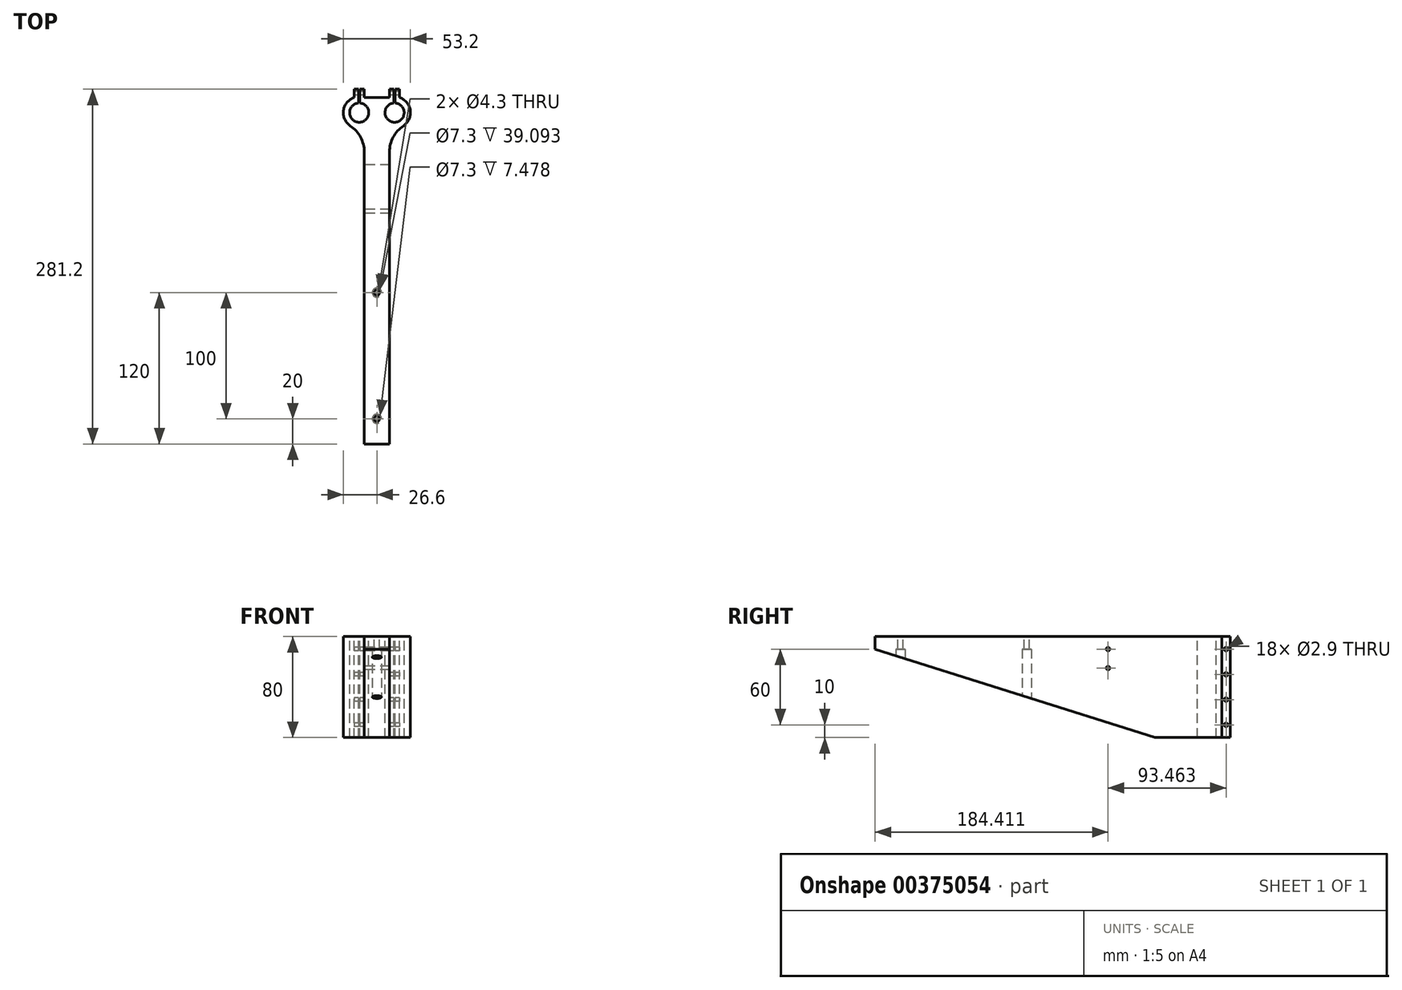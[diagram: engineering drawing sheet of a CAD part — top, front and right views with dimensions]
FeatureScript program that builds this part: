
annotation { "Feature Type Name" : "Feature", "Feature Type Description" : "" }
export const myFeature = defineFeature(function(context is Context, id is Id, definition is map)
    precondition{}
    {
        {
            var Q0;
            Q0=qCreatedBy(makeId("Top.planeOp"),FACE);
            var sketch = newSketch(context, id + "F0", { "sketchPlane" : qUnion([Q0])});
            skCircle(sketch, "E0", {"center": v(0, 0) * mm, "radius": 7.6 * mm});
            skArc(sketch, "E1.0", {"start": v(-4, 11.95) * mm, "mid": v(-12.49, 1.7) * mm, "end": v(-7.04, -10.45) * mm});
            skLineSegment(sketch, "E2.top", {"start": v(4, 18.6) * mm, "end": v(-4, 18.6) * mm});
            skLineSegment(sketch, "E2.left", {"start": v(4, 11.95) * mm, "end": v(4, 18.6) * mm});
            skLineSegment(sketch, "E2.right", {"start": v(-4, 11.95) * mm, "end": v(-4, 18.6) * mm});
            skPoint(sketch, "E2.middle", {"position": v(0, 12.6) * mm});
            skLineSegment(sketch, "E3.top", {"start": v(4, -262.6) * mm, "end": v(24, -262.6) * mm});
            skCircle(sketch, "E4", {"center": v(28, 0) * mm, "radius": 7.6 * mm});
            skArc(sketch, "E5.0", {"start": v(35.04, -10.45) * mm, "mid": v(40.49, 1.7) * mm, "end": v(32, 11.95) * mm});
            skLineSegment(sketch, "E6.bottom", {"start": v(24, 18.6) * mm, "end": v(32, 18.6) * mm});
            skLineSegment(sketch, "E6.left", {"start": v(24, 18.6) * mm, "end": v(24, 11.95) * mm});
            skLineSegment(sketch, "E6.right", {"start": v(32, 18.6) * mm, "end": v(32, 11.95) * mm});
            skLineSegment(sketch, "E7", {"start": v(4, 11.95) * mm, "end": v(24, 11.95) * mm});
            skLineSegment(sketch, "E8", {"start": v(4, -31.19) * mm, "end": v(4, -262.6) * mm});
            skLineSegment(sketch, "E9", {"start": v(24, -262.6) * mm, "end": v(24, -31.19) * mm});
            skPoint(sketch, "E10.visualSharp", {"position": v(4, -11.95) * mm});
            skArc(sketch, "E10.filletArc", {"start": v(4, -31.19) * mm, "mid": v(1.07, -19.44) * mm, "end": v(-7.04, -10.45) * mm});
            skPoint(sketch, "E11.visualSharp", {"position": v(24, -11.95) * mm});
            skArc(sketch, "E11.filletArc", {"start": v(35.04, -10.45) * mm, "mid": v(26.93, -19.44) * mm, "end": v(24, -31.19) * mm});
            skSolve(sketch);
        }
        {
            var Q0;
            Q0=makeQuery(id+"F0.imprint","IMPRINT",FACE,{"disambiguationData":[TD([[makeQuery(id+"F0.imprint","IMPRINT",EDGE,{"derivedFrom":sQuery(id+"F0.wireOp",EDGE,"E3.top")}),1.0]])]});
            extrude(context, id + "F1", {"entities" : qUnion([Q0]), "oppositeDirection" : true, "depth" : 80 * mm});
        }
        {
            var Q0;
            Q0=makeQuery(id+"F0.imprint","IMPRINT",FACE,{"disambiguationData":[TD([[makeQuery(id+"F0.imprint","IMPRINT",EDGE,{"derivedFrom":sQuery(id+"F0.wireOp",EDGE,"E0")}),-1.0]])]});
            extrude(context, id + "F2", {"entities" : qUnion([Q0]), "operationType" : NewBodyOperationType.ADD, "oppositeDirection" : true, "depth" : 80 * mm});
        }
        {
            var Q0;
            {var subQ0=sQuery(id+"F0.wireOp",EDGE,"E1.0");Q0=makeQuery(id+"F2.boolean.opBoolean","MERGE",FACE,{"derivedFrom":[makeQuery(id+"F1.opExtrude","CAP_FACE",FACE,{"disambiguationData":[OSD([subQ0,sQuery(id+"F0.wireOp",EDGE,"E3.top"),sQuery(id+"F0.wireOp",EDGE,"E3.left"),sQuery(id+"F0.wireOp",EDGE,"E3.right")])],"isStart":true}),makeQuery(id+"F2.opExtrude","CAP_FACE",FACE,{"disambiguationData":[OSD([sQuery(id+"F0.wireOp",EDGE,"E0"),subQ0,sQuery(id+"F0.wireOp",EDGE,"E2.top"),sQuery(id+"F0.wireOp",EDGE,"E2.left"),sQuery(id+"F0.wireOp",EDGE,"E2.right")])],"isStart":true})]});}
            var sketch = newSketch(context, id + "F3", { "sketchPlane" : qUnion([Q0])});
            skCircle(sketch, "E12", {"center": v(14, -142.6) * mm, "radius": 2.15 * mm});
            skCircle(sketch, "E13", {"center": v(14, -242.6) * mm, "radius": 2.15 * mm});
            skSolve(sketch);
        }
        {
            var Q0;
            Q0=qSketchRegion(id+"F3",true);
            extrude(context, id + "F4", {"entities" : qUnion([Q0]), "operationType" : NewBodyOperationType.REMOVE, "endBound" : BoundingType.THROUGH_ALL, "oppositeDirection" : true, "depth" : 25 * mm});
        }
        {
            var Q0;
            Q0=makeQuery(id+"F1.opExtrude","CAP_FACE",FACE,{"disambiguationData":[OSD([sQuery(id+"F0.wireOp",EDGE,"E0"),sQuery(id+"F0.wireOp",EDGE,"E1.0"),sQuery(id+"F0.wireOp",EDGE,"E2.top"),sQuery(id+"F0.wireOp",EDGE,"E2.left"),sQuery(id+"F0.wireOp",EDGE,"E2.right"),sQuery(id+"F0.wireOp",EDGE,"E3.top"),sQuery(id+"F0.wireOp",EDGE,"E3.left"),sQuery(id+"F0.wireOp",EDGE,"E3.right")])],"isStart":false});
            var sketch = newSketch(context, id + "F5", { "sketchPlane" : qUnion([Q0])});
            skCircle(sketch, "E14", {"center": v(14, 242.6) * mm, "radius": 3.65 * mm});
            skCircle(sketch, "E15", {"center": v(14, 142.6) * mm, "radius": 3.65 * mm});
            skSolve(sketch);
        }
        {
            var Q0;
            Q0=makeQuery(id+"F5.imprint","IMPRINT",FACE,{"disambiguationData":[TD([[makeQuery(id+"F5.imprint","IMPRINT",EDGE,{"derivedFrom":sQuery(id+"F5.wireOp",EDGE,"E14")}),1.0]])]});
            var Q1;
            Q1=makeQuery(id+"F5.imprint","IMPRINT",FACE,{"disambiguationData":[TD([[makeQuery(id+"F5.imprint","IMPRINT",EDGE,{"derivedFrom":sQuery(id+"F5.wireOp",EDGE,"E15")}),1.0]])]});
            extrude(context, id + "F6", {"entities" : qUnion([Q0, Q1]), "operationType" : NewBodyOperationType.REMOVE, "oppositeDirection" : true, "depth" : (80 - 10) * mm});
        }
        {
            var Q0;
            Q0=makeQuery(id+"F1.opExtrude","SWEPT_FACE",FACE,{"disambiguationData":[OSD([sQuery(id+"F0.wireOp",EDGE,"E8")])]});
            var sketch = newSketch(context, id + "F7", { "sketchPlane" : qUnion([Q0])});
            skLineSegment(sketch, "E16", {"start": v(262.6, 0) * mm, "end": v(262.6, -10) * mm});
            skLineSegment(sketch, "E17", {"start": v(31.19, -80) * mm, "end": v(41.19, -80) * mm});
            skLineSegment(sketch, "E18", {"start": v(262.6, -10) * mm, "end": v(41.19, -80) * mm});
            skSolve(sketch);
        }
        {
            var Q0;
            {var subQ0=sQuery(id+"F7.wireOp",EDGE,"E18");Q0=makeQuery(id+"F7.imprint","IMPRINT",FACE,{"disambiguationData":[TD([[makeQuery(id+"F7.imprint","IMPRINT",EDGE,{"derivedFrom":subQ0}),1.0]])]});}
            extrude(context, id + "F8", {"entities" : qUnion([Q0]), "operationType" : NewBodyOperationType.REMOVE, "endBound" : BoundingType.THROUGH_ALL, "oppositeDirection" : true, "depth" : 25 * mm});
        }
        {
            var Q0;
            Q0=makeQuery(id+"F1.opExtrude","CAP_FACE",FACE,{"disambiguationData":[OSD([sQuery(id+"F0.wireOp",EDGE,"E0"),sQuery(id+"F0.wireOp",EDGE,"E1.0"),sQuery(id+"F0.wireOp",EDGE,"E2.top"),sQuery(id+"F0.wireOp",EDGE,"E2.left"),sQuery(id+"F0.wireOp",EDGE,"E2.right"),sQuery(id+"F0.wireOp",EDGE,"E3.top"),sQuery(id+"F0.wireOp",EDGE,"E3.left"),sQuery(id+"F0.wireOp",EDGE,"E3.right")])],"isStart":true});
            var sketch = newSketch(context, id + "F9", { "sketchPlane" : qUnion([Q0])});
            skLineSegment(sketch, "E19.bottom", {"start": v(0, 18.6) * mm, "end": v(-0.5, 18.6) * mm});
            skLineSegment(sketch, "E19.top", {"start": v(0, 0) * mm, "end": v(-0.5, 0) * mm});
            skLineSegment(sketch, "E19.left", {"start": v(0, 18.6) * mm, "end": v(0, 0) * mm});
            skLineSegment(sketch, "E19.right", {"start": v(-0.5, 18.6) * mm, "end": v(-0.5, 0) * mm});
            skLineSegment(sketch, "E20.MirrorCS", {"start": v(0.5, 18.6) * mm, "end": v(0.5, 0) * mm});
            skLineSegment(sketch, "E21.MirrorCS", {"start": v(0, 0) * mm, "end": v(0.5, 0) * mm});
            skLineSegment(sketch, "E22.MirrorCS", {"start": v(0, 18.6) * mm, "end": v(0.5, 18.6) * mm});
            skLineSegment(sketch, "E23", {"start": v(14, 11.95) * mm, "end": v(14, -10.83) * mm, "construction": true});
            skLineSegment(sketch, "E24.MirrorCS", {"start": v(28, 18.6) * mm, "end": v(27.5, 18.6) * mm});
            skLineSegment(sketch, "E25.MirrorCS", {"start": v(28, 18.6) * mm, "end": v(28.5, 18.6) * mm});
            skLineSegment(sketch, "E26.MirrorCS", {"start": v(28, 0) * mm, "end": v(27.5, 0) * mm});
            skLineSegment(sketch, "E27.MirrorCS", {"start": v(28, 0) * mm, "end": v(28.5, 0) * mm});
            skLineSegment(sketch, "E28.MirrorCS", {"start": v(28, 18.6) * mm, "end": v(28, 0) * mm});
            skLineSegment(sketch, "E29.MirrorCS", {"start": v(28.5, 18.6) * mm, "end": v(28.5, 0) * mm});
            skLineSegment(sketch, "E30.MirrorCS", {"start": v(27.5, 18.6) * mm, "end": v(27.5, 0) * mm});
            skSolve(sketch);
        }
        {
            var Q0;
            Q0=qSketchRegion(id+"F9",true);
            extrude(context, id + "F10", {"entities" : qUnion([Q0]), "operationType" : NewBodyOperationType.REMOVE, "endBound" : BoundingType.THROUGH_ALL, "oppositeDirection" : true, "depth" : 25 * mm});
        }
        {
            var Q0;
            Q0=makeQuery(id+"F1.opExtrude","SWEPT_FACE",FACE,{"disambiguationData":[OSD([sQuery(id+"F0.wireOp",EDGE,"E2.right")])]});
            var sketch = newSketch(context, id + "F11", { "sketchPlane" : qUnion([Q0])});
            skCircle(sketch, "E31", {"center": v(-15.27, -30) * mm, "radius": 1.45 * mm});
            skCircle(sketch, "E32", {"center": v(-15.27, -70) * mm, "radius": 1.45 * mm});
            skCircle(sketch, "E33.0", {"center": v(-15.27, -30) * mm, "radius": 2.45 * mm});
            skCircle(sketch, "E34.0", {"center": v(-15.27, -70) * mm, "radius": 2.45 * mm});
            skCircle(sketch, "E35", {"center": v(-15.27, -10) * mm, "radius": 1.45 * mm});
            skCircle(sketch, "E36", {"center": v(-15.27, -10) * mm, "radius": 2.45 * mm});
            skCircle(sketch, "E37", {"center": v(-15.27, -50) * mm, "radius": 1.45 * mm});
            skCircle(sketch, "E38", {"center": v(-15.27, -50) * mm, "radius": 2.45 * mm});
            skSolve(sketch);
        }
        {
            var Q0;
            Q0=makeQuery(id+"F11.imprint","IMPRINT",FACE,{"disambiguationData":[TD([[makeQuery(id+"F11.imprint","IMPRINT",EDGE,{"derivedFrom":sQuery(id+"F11.wireOp",EDGE,"E31")}),1.0]])]});
            var Q1;
            Q1=makeQuery(id+"F11.imprint","IMPRINT",FACE,{"disambiguationData":[TD([[makeQuery(id+"F11.imprint","IMPRINT",EDGE,{"derivedFrom":sQuery(id+"F11.wireOp",EDGE,"E32")}),1.0]])]});
            var Q2;
            Q2=makeQuery(id+"F11.imprint","IMPRINT",FACE,{"disambiguationData":[TD([[makeQuery(id+"F11.imprint","IMPRINT",EDGE,{"derivedFrom":sQuery(id+"F11.wireOp",EDGE,"E37")}),1.0]])]});
            var Q3;
            Q3=makeQuery(id+"F11.imprint","IMPRINT",FACE,{"disambiguationData":[TD([[makeQuery(id+"F11.imprint","IMPRINT",EDGE,{"derivedFrom":sQuery(id+"F11.wireOp",EDGE,"E35")}),1.0]])]});
            extrude(context, id + "F12", {"entities" : qUnion([Q0, Q1, Q2, Q3]), "operationType" : NewBodyOperationType.REMOVE, "endBound" : BoundingType.THROUGH_ALL, "oppositeDirection" : true, "depth" : 25 * mm});
        }
        {
            var Q0;
            Q0=makeQuery(id+"F1.opExtrude","SWEPT_FACE",FACE,{"disambiguationData":[OSD([sQuery(id+"F0.wireOp",EDGE,"E8")])]});
            var sketch = newSketch(context, id + "F13", { "sketchPlane" : qUnion([Q0])});
            skCircle(sketch, "E39", {"center": v(78.19, -10) * mm, "radius": 1.45 * mm});
            skCircle(sketch, "E40", {"center": v(78.19, -25) * mm, "radius": 1.45 * mm});
            skSolve(sketch);
        }
        {
            var Q0;
            Q0=makeQuery(id+"F13.imprint","IMPRINT",FACE,{"disambiguationData":[TD([[makeQuery(id+"F13.imprint","IMPRINT",EDGE,{"derivedFrom":sQuery(id+"F13.wireOp",EDGE,"E39")}),1.0]])]});
            var Q1;
            Q1=makeQuery(id+"F13.imprint","IMPRINT",FACE,{"disambiguationData":[TD([[makeQuery(id+"F13.imprint","IMPRINT",EDGE,{"derivedFrom":sQuery(id+"F13.wireOp",EDGE,"E40")}),1.0]])]});
            extrude(context, id + "F14", {"entities" : qUnion([Q0, Q1]), "operationType" : NewBodyOperationType.REMOVE, "endBound" : BoundingType.THROUGH_ALL, "oppositeDirection" : true, "depth" : 25 * mm});
        }
    });
